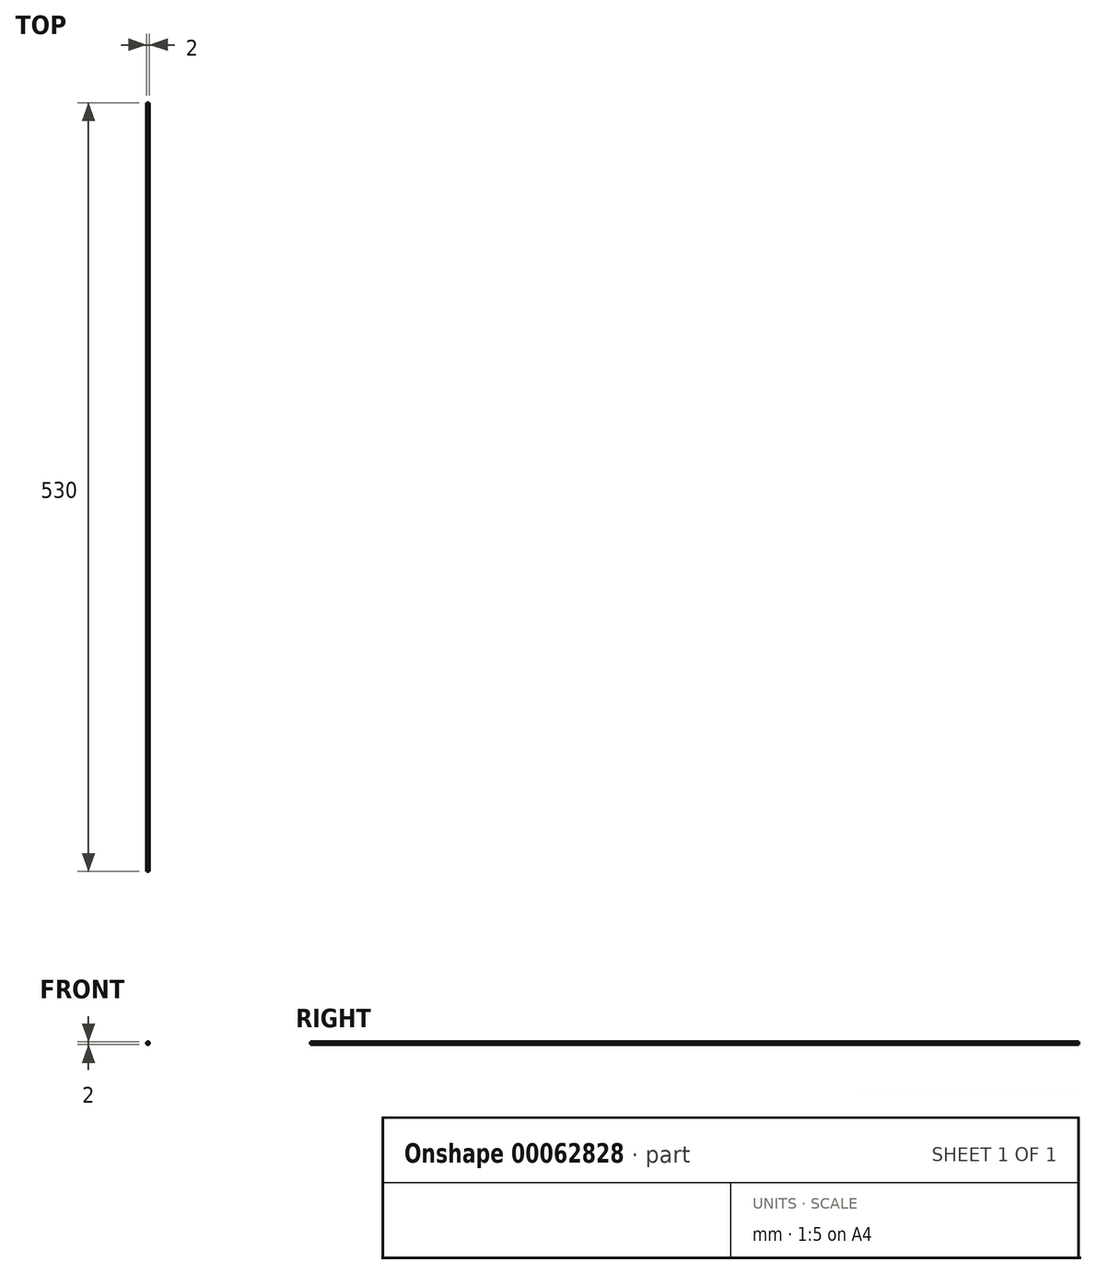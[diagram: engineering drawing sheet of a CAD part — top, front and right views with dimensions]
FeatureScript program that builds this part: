
annotation { "Feature Type Name" : "Feature", "Feature Type Description" : "" }
export const myFeature = defineFeature(function(context is Context, id is Id, definition is map)
    precondition{}
    {
        {
            var Q0;
            Q0=qCreatedBy(makeId("Front.planeOp"),FACE);
            var sketch = newSketch(context, id + "F0", { "sketchPlane" : qUnion([Q0])});
            skCircle(sketch, "E0", {"center": v(0, 0) * mm, "radius": 1 * mm});
            skSolve(sketch);
        }
        {
            var Q0;
            Q0 = qSketchRegion(id + "F0", true);
            extrude(context, id + "F1", {"entities" : qUnion([Q0]), "depth" : 530 * mm});
        }
    });
